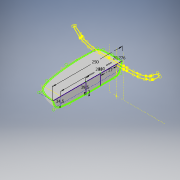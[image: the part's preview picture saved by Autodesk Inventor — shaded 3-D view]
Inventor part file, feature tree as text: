
AUTODESK INVENTOR PART (.ipt)
format: ipt  version: 2019.3 (Build 233278000, 278)  size: 3,379,712 bytes
history: native  units: mm
features: other x20, surface_op x5, sketch x3, plane x3, loft x2
ambient origin geometry x8: Origin, YZ Plane, XZ Plane, XY Plane, X Axis, Y Axis, Z Axis, Center Point
bodies: Body1 (feature_tree), Body2 (feature_tree), Body3 (feature_tree), Body4 (feature_tree), Body5 (feature_tree), Body6 (feature_tree), Body7 (feature_tree), Body8 (feature_tree), Body9 (feature_tree), Body10 (feature_tree), Body11 (feature_tree), Body12 (feature_tree), Body13 (feature_tree), Body14 (feature_tree), Body15 (feature_tree), Body16 (feature_tree), Body17 (feature_tree), Body18 (feature_tree), Body19 (feature_tree), Body20 (feature_tree), Body21 (feature_tree), Body22 (feature_tree)
feature tree (33):
  other  "deck.ipt"
  sketch  "Sketch1"  dims[d15=212.0mm d47=28.0mm]
  sketch  "Sketch2"  dims[d48=145.0mm d107=200.0mm]
  sketch  "Sketch3"  dims[d108=10.0mm d122=84.0mm d130=110.0mm d144=25.0mm d145=25.0mm d150=63.0mm d190=35.5mm d191=38.8mm d192=39.5mm d193=34.5mm d194=110.0mm d195=200.0mm d196=81.0mm d197=25.0mm d199=20.776473mm d316=3.0mm d321=3.0mm d423=140.0mm d425=205.0mm d429=141.0mm d430=250.0mm d455=57.0mm d472=0.0mm d473=90.0deg d474=0.0mm d475=90.0deg d476=0.0mm d477=90.0deg d478=0.0mm d479=90.0deg d499=3.0mm d506=0.0mm d507=90.0deg d508=0.0mm d509=90.0deg d510=0.0mm d511=90.0deg d512=0.0mm d513=90.0deg]
  other  "Transversal (front)"
  other  "Longitudinal"
  plane  "Work Plane9"
  other  "Transversal (mid)"
  plane  "Work Plane1"
  other  "Transversal (back)"
  plane  "Work Plane7"
  other  "Top"
  loft  "Loft5"
  other  "Image2"
  other  "Image3"
  other  "Image4"
  other  "Front Profile"
  other  "Srf48"
  other  "Srf49"
  other  "Srf50"
  other  "Edges59"
  other  "Edges60"
  other  "Srf51"
  other  "Srf52"
  other  "Srf53"
  other  "Edges61"
  other  "Edges62"
  loft  "LoftSrf13"
  surface_op  "Boundary Patch25"
  surface_op  "Boundary Patch26"
  surface_op  "Boundary Patch27"
  surface_op  "Boundary Patch28"
  surface_op  "Boundary Patch29"
